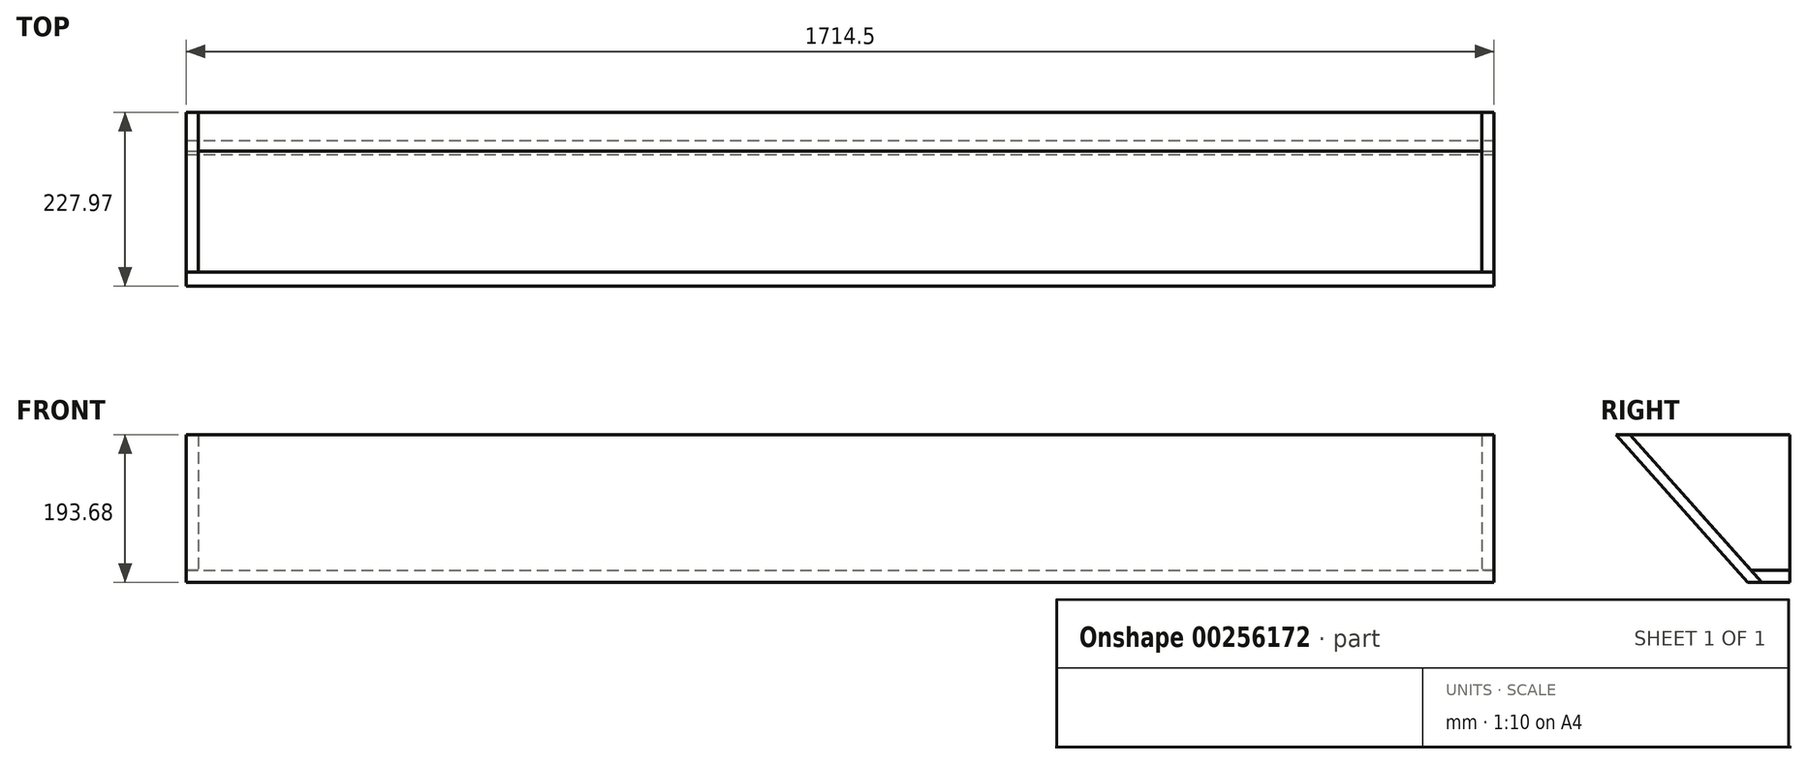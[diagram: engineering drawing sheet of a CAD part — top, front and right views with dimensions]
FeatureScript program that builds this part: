
annotation { "Feature Type Name" : "Feature", "Feature Type Description" : "" }
export const myFeature = defineFeature(function(context is Context, id is Id, definition is map)
    precondition{}
    {
        {
            var Q0;
            Q0=qCreatedBy(makeId("Right.planeOp"),FACE);
            var sketch = newSketch(context, id + "F0", { "sketchPlane" : qUnion([Q0])});
            skLineSegment(sketch, "E0", {"start": v(0, 0) * mm, "end": v(-50.8, 0) * mm});
            skLineSegment(sketch, "E1", {"start": v(-50.8, 0) * mm, "end": v(-209.55, 177.8) * mm});
            skLineSegment(sketch, "E2", {"start": v(-209.55, 177.8) * mm, "end": v(0, 177.8) * mm});
            skLineSegment(sketch, "E3", {"start": v(0, 177.8) * mm, "end": v(0, 0) * mm});
            skSolve(sketch);
        }
        {
            var Q0;
            Q0 = qSketchRegion(id + "F0", true);
            extrude(context, id + "F1", {"entities" : qUnion([Q0]), "depth" : 15.88 * mm});
        }
        {
            var Q0;
            Q0=makeQuery(id+"F1.opExtrude","CAP_FACE",FACE,{"disambiguationData":[OSD([sQuery(id+"F0.wireOp",EDGE,"E0"),sQuery(id+"F0.wireOp",EDGE,"E1"),sQuery(id+"F0.wireOp",EDGE,"E2"),sQuery(id+"F0.wireOp",EDGE,"E3")])],"isStart":false});
            var sketch = newSketch(context, id + "F2", { "sketchPlane" : qUnion([Q0])});
            skSolve(sketch);
        }
        {
            var Q0;
            Q0=makeQuery(id+"F2.imprint","IMPRINT",FACE,{"disambiguationData":[TD([[makeQuery(id+"F2.imprint","IMPRINT",EDGE,{"derivedFrom":makeQuery(id+"F1.opExtrude","CAP_EDGE",EDGE,{"disambiguationData":[OSD([sQuery(id+"F0.wireOp",EDGE,"E0")])],"isStart":false})}),-1.0]])]});
            var sketch = newSketch(context, id + "F3", { "sketchPlane" : qUnion([Q0])});
            skLineSegment(sketch, "E4", {"start": v(0, 0) * mm, "end": v(0, -15.88) * mm});
            skLineSegment(sketch, "E5", {"start": v(0, -15.88) * mm, "end": v(-36.63, -15.88) * mm});
            skLineSegment(sketch, "E6", {"start": v(-36.63, -15.88) * mm, "end": v(-50.8, 0) * mm});
            skLineSegment(sketch, "E7", {"start": v(-50.8, 0) * mm, "end": v(0, 0) * mm});
            skSolve(sketch);
        }
        {
            var Q0;
            Q0 = qSketchRegion(id + "F3", true);
            extrude(context, id + "F4", {"entities" : qUnion([Q0]), "oppositeDirection" : true, "depth" : 1714.5 * mm});
        }
        {
            var Q0;
            Q0=makeQuery(id+"F2.imprint","IMPRINT",FACE,{"disambiguationData":[TD([[makeQuery(id+"F2.imprint","IMPRINT",EDGE,{"derivedFrom":makeQuery(id+"F1.opExtrude","CAP_EDGE",EDGE,{"disambiguationData":[OSD([sQuery(id+"F0.wireOp",EDGE,"E0")])],"isStart":false})}),-1.0]])]});
            var sketch = newSketch(context, id + "F5", { "sketchPlane" : qUnion([Q0])});
            skLineSegment(sketch, "E8", {"start": v(-209.55, 177.8) * mm, "end": v(-227.97, 177.8) * mm});
            skLineSegment(sketch, "E9", {"start": v(-227.97, 177.8) * mm, "end": v(-55.05, -15.88) * mm});
            skLineSegment(sketch, "E10", {"start": v(-55.05, -15.88) * mm, "end": v(-36.63, -15.88) * mm});
            skLineSegment(sketch, "E11", {"start": v(-36.63, -15.88) * mm, "end": v(-209.55, 177.8) * mm});
            skSolve(sketch);
        }
        {
            var Q0;
            Q0 = qSketchRegion(id + "F5", true);
            extrude(context, id + "F6", {"entities" : qUnion([Q0]), "oppositeDirection" : true, "depth" : 1714.5 * mm});
        }
        {
            var Q0;
            Q0=makeQuery(id+"F1.opExtrude","SWEPT_BODY",BODY,{"disambiguationData":[OSD([sQuery(id+"F0.wireOp",EDGE,"E0"),sQuery(id+"F0.wireOp",EDGE,"E1"),sQuery(id+"F0.wireOp",EDGE,"E2"),sQuery(id+"F0.wireOp",EDGE,"E3")])]});
            transform(context, id + "F7", {"entities" : qUnion([Q0]), "transformType" : TransformType.TRANSLATION_3D, "dx" : -1698.62 * mm, "dy" : 0 * mm, "dz" : 0 * mm, "makeCopy" : true});
        }
    });
